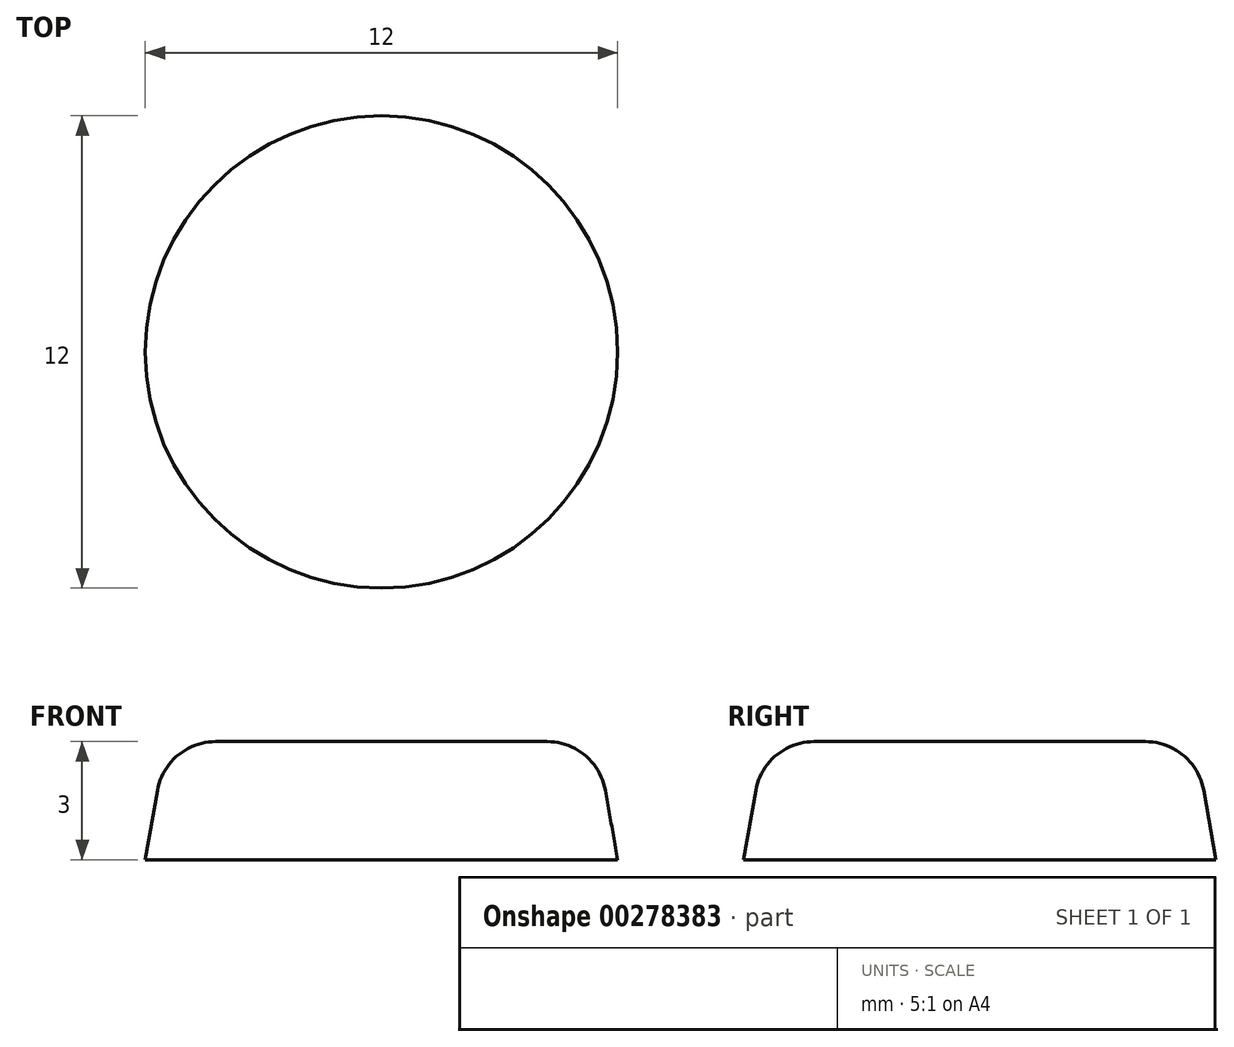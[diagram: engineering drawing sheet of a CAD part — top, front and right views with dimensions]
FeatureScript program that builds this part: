
annotation { "Feature Type Name" : "Feature", "Feature Type Description" : "" }
export const myFeature = defineFeature(function(context is Context, id is Id, definition is map)
    precondition{}
    {
        {
            var Q0;
            Q0=qCreatedBy(makeId("Top.planeOp"),FACE);
            var sketch = newSketch(context, id + "F0", { "sketchPlane" : qUnion([Q0])});
            skCircle(sketch, "E0", {"center": v(0, 0) * mm, "radius": 6 * mm});
            skSolve(sketch);
        }
        {
            var Q0;
            Q0=makeQuery(id+"F0.imprint","IMPRINT",FACE,{"disambiguationData":[TD([[makeQuery(id+"F0.imprint","IMPRINT",EDGE,{"derivedFrom":sQuery(id+"F0.wireOp",EDGE,"E0")}),1.0]])]});
            extrude(context, id + "F1", {"entities" : qUnion([Q0]), "depth" : 3 * mm, "hasDraft" : true, "draftAngle" : 10 * degree, "draftPullDirection" : true});
        }
        {
            var Q0;
            Q0=makeQuery(id+"F1.opExtrude","CAP_EDGE",EDGE,{"disambiguationData":[OSD([sQuery(id+"F0.wireOp",EDGE,"E0")])],"isStart":false});
            fillet(context, id + "F2", {"entities" : qUnion([Q0]), "radius" : 1.5 * mm, "tangentPropagation" : true, "allowEdgeOverflow" : false});
        }
    });
